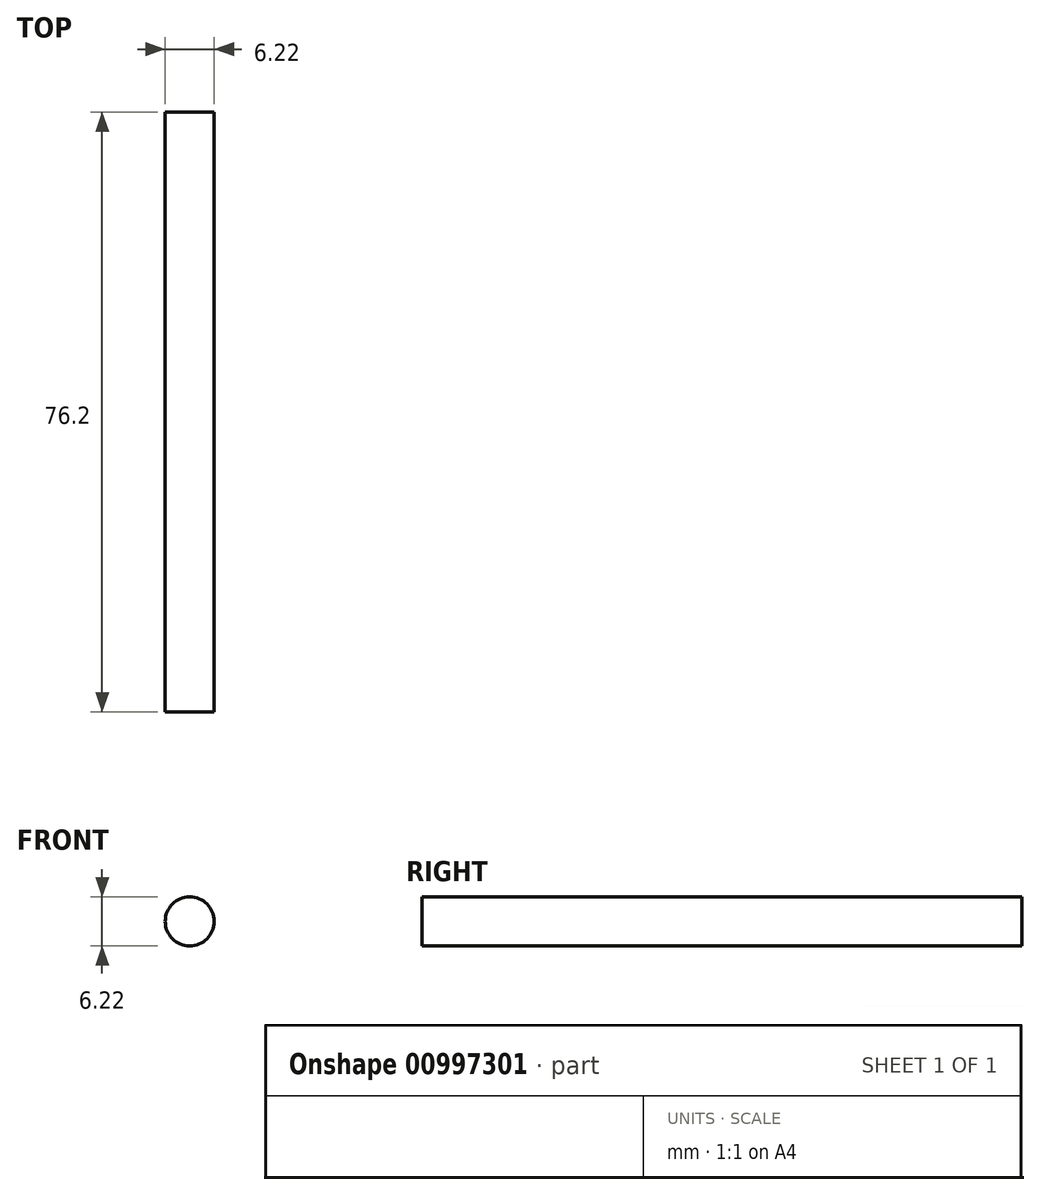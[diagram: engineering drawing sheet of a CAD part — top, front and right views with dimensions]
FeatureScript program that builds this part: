
annotation { "Feature Type Name" : "Feature", "Feature Type Description" : "" }
export const myFeature = defineFeature(function(context is Context, id is Id, definition is map)
    precondition{}
    {
        {
            var Q0;
            Q0=qCreatedBy(makeId("Front.planeOp"),FACE);
            var sketch = newSketch(context, id + "F0", { "sketchPlane" : qUnion([Q0])});
            skCircle(sketch, "E0", {"center": v(0, 0) * mm, "radius": 3.11 * mm});
            skSolve(sketch);
        }
        {
            var Q0;
            Q0=makeQuery(id+"F0.imprint","IMPRINT",FACE,{"disambiguationData":[TD([[makeQuery(id+"F0.imprint","IMPRINT",EDGE,{"derivedFrom":sQuery(id+"F0.wireOp",EDGE,"E0")}),1.0]])]});
            var Q1;
            Q1=sQuery(id+"F0.wireOp",EDGE,"E0");
            extrude(context, id + "F1", {"entities" : qUnion([Q0]), "surfaceEntities" : qUnion([Q1]), "depth" : 76.2 * mm, "offsetDistance" : 25.4 * mm, "symmetric" : true});
        }
    });
